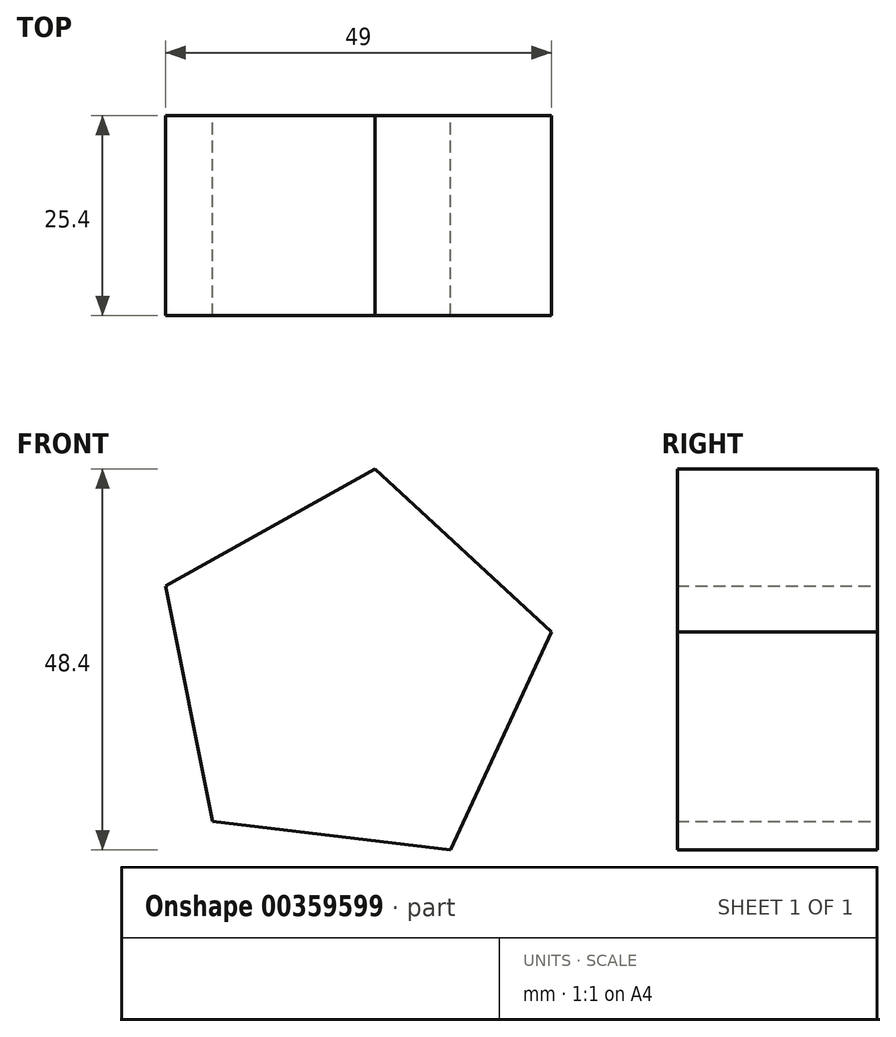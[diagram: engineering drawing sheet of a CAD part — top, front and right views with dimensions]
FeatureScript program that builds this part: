
annotation { "Feature Type Name" : "Feature", "Feature Type Description" : "" }
export const myFeature = defineFeature(function(context is Context, id is Id, definition is map)
    precondition{}
    {
        {
            var Q0;
            Q0=qCreatedBy(makeId("Front.planeOp"),FACE);
            var sketch = newSketch(context, id + "F0", { "sketchPlane" : qUnion([Q0])});
            skCircle(sketch, "E0.cCircle", {"center": v(0, 0) * mm, "radius": 20.99 * mm, "construction": true});
            skLineSegment(sketch, "E0.0", {"start": v(-23.55, 10.88) * mm, "end": v(3.07, 25.76) * mm});
            skLineSegment(sketch, "E0.1", {"start": v(3.07, 25.76) * mm, "end": v(25.45, 5.04) * mm});
            skLineSegment(sketch, "E0.2", {"start": v(25.45, 5.04) * mm, "end": v(12.65, -22.64) * mm});
            skLineSegment(sketch, "E0.3", {"start": v(12.65, -22.64) * mm, "end": v(-17.62, -19.03) * mm});
            skLineSegment(sketch, "E0.4", {"start": v(-17.62, -19.03) * mm, "end": v(-23.55, 10.88) * mm});
            skPoint(sketch, "E0.0.midPoint", {"position": v(-10.24, 18.32) * mm});
            skSolve(sketch);
        }
        {
            var Q0;
            Q0 = qSketchRegion(id + "F0", true);
            extrude(context, id + "F1", {"entities" : qUnion([Q0]), "depth" : 25.4 * mm});
        }
    });
